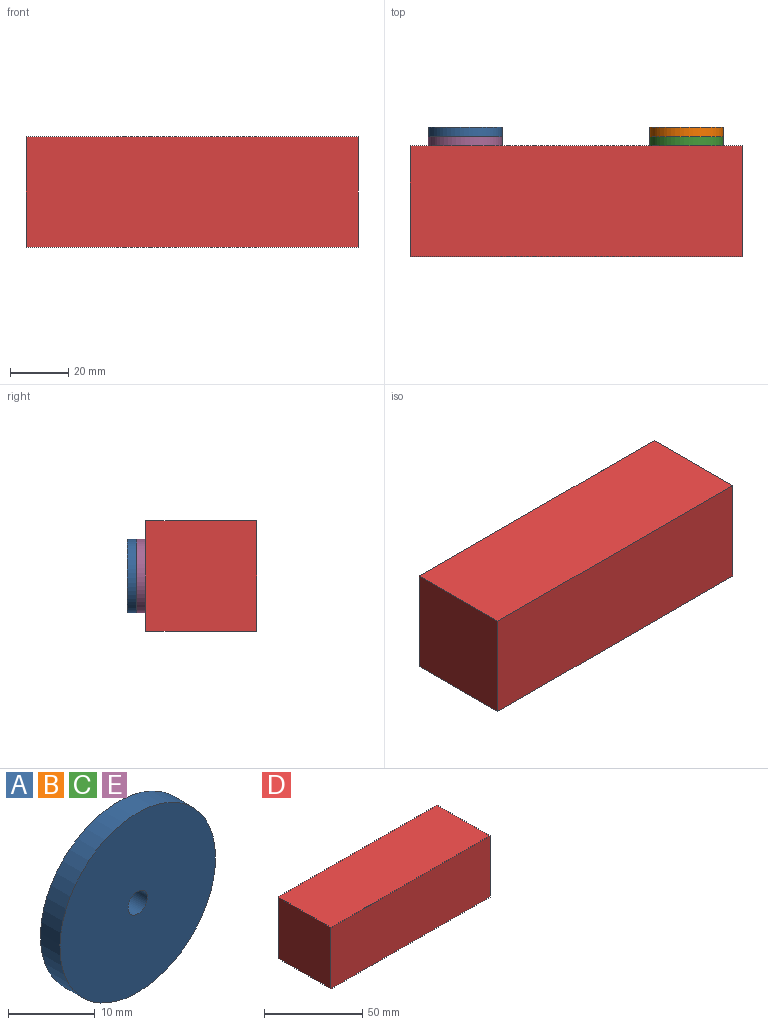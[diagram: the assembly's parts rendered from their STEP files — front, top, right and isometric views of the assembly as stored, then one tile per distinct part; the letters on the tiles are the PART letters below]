
ASSEMBLY  parts=5 mates=4
PART A: 4 faces, bbox 25.4x3.2x25.4 mm
  f0: cylinder r=1.59mm len=3.18mm, axis (0,1,0), area 31.7mm2, adj f2,f3
  f1: cylinder r=12.7mm len=25.4mm, axis (0,1,0), area 253.4mm2, adj f2,f3
  f2: plane 25.4x25.4mm, normal (0,-1,0), area 498.8mm2, adj f0,f1
  f3: plane 25.4x25.4mm, normal (0,1,0), area 498.8mm2, adj f0,f1
PART B: same geometry as A
PART C: same geometry as A
PART D: 6 faces, bbox 114.3x38.1x38.1 mm
  f0: plane 114.3x38.1mm, normal (0,1,0), area 4354.8mm2, adj f1,f3,f4,f5
  f1: plane 114.3x38.1mm, normal (0,0,1), area 4354.8mm2, adj f0,f2,f4,f5
  f2: plane 114.3x38.1mm, normal (0,-1,0), area 4354.8mm2, adj f1,f3,f4,f5
  f3: plane 114.3x38.1mm, normal (0,0,-1), area 4354.8mm2, adj f0,f2,f4,f5
  f4: plane 38.1x38.1mm, normal (1,0,0), area 1451.6mm2, adj f0,f1,f2,f3
  f5: plane 38.1x38.1mm, normal (-1,0,0), area 1451.6mm2, adj f0,f1,f2,f3
PART E: same geometry as A
PLACE A rot(axis=(0.29,0,-0.96),180deg) t=(-38.1,22.23,-19.05)mm
PLACE B t=(38.1,25.4,-19.05)mm
PLACE C t=(38.1,22.23,-19.05)mm
PLACE D t=(-57.15,0,-19.05)mm
PLACE E rot(axis=(1,0,0),180deg) t=(-38.1,19.05,-19.05)mm
MATE fastened E.f1 <-> D.f0  axis (0,-1,0) through (-38.1,19.05,-19.05)mm
MATE revolute B.f1 <-> C.f1  axis (0,-1,0) through (38.1,22.23,-19.05)mm
MATE revolute A.f1 <-> E.f1  axis (0,-1,0) through (-38.1,22.23,-19.05)mm
MATE fastened C.f1 <-> D.f0  axis (0,-1,0) through (38.1,19.05,-19.05)mm
